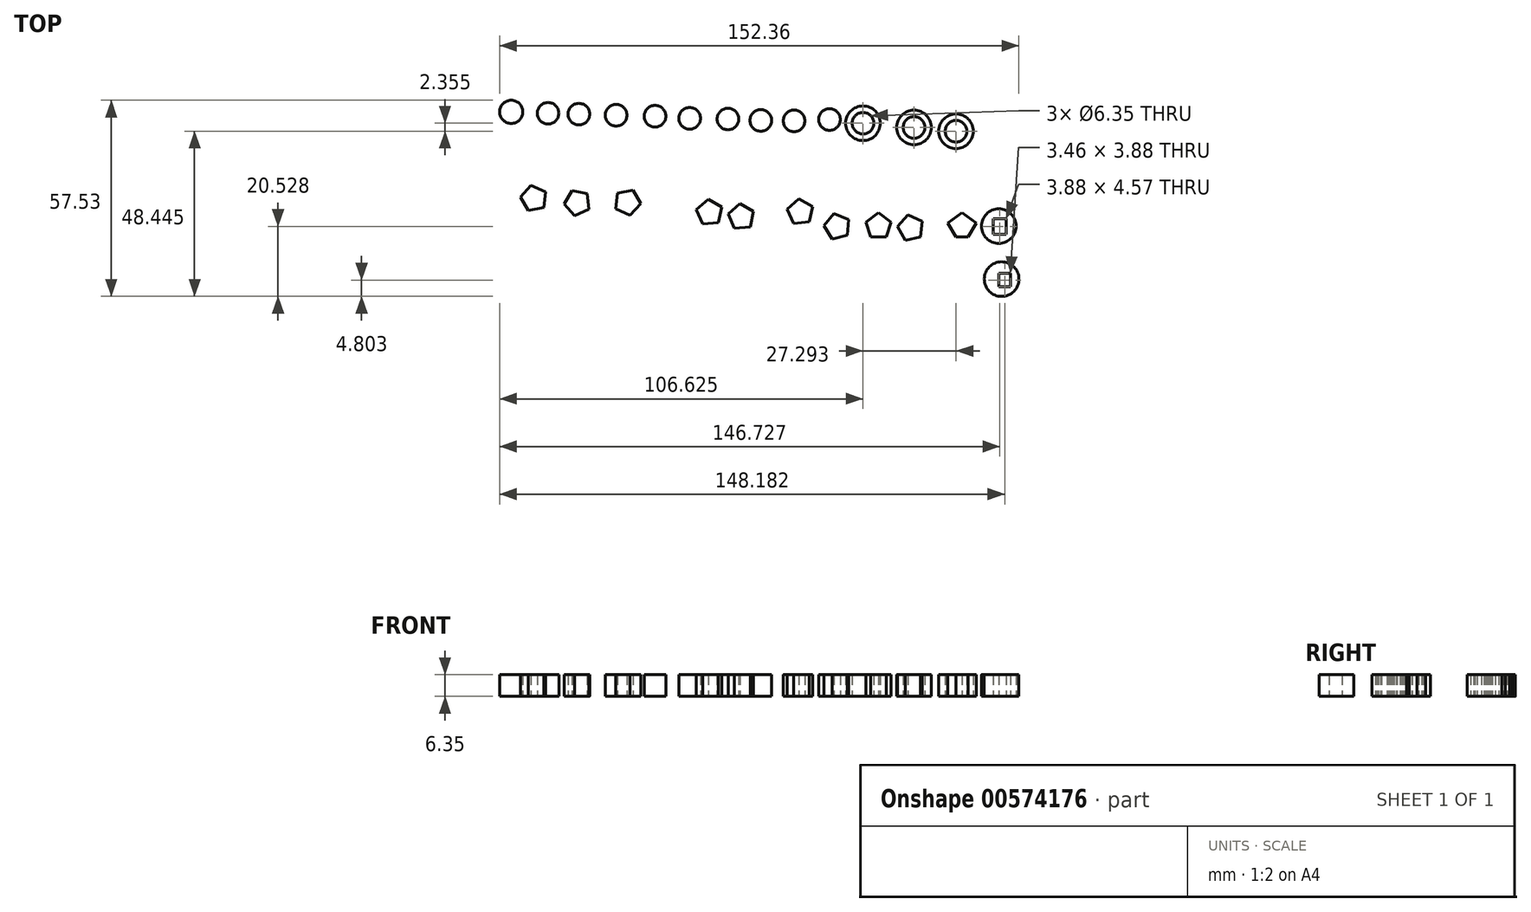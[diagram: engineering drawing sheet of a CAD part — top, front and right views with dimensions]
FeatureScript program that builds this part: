
annotation { "Feature Type Name" : "Feature", "Feature Type Description" : "" }
export const myFeature = defineFeature(function(context is Context, id is Id, definition is map)
    precondition{}
    {
        {
            var Q0;
            Q0=qCreatedBy(makeId("Top.planeOp"),FACE);
            var sketch = newSketch(context, id + "F0", { "sketchPlane" : qUnion([Q0])});
            skCircle(sketch, "E0", {"center": v(-53.37, 48.39) * mm, "radius": 3.18 * mm});
            skCircle(sketch, "E1", {"center": v(-42.44, 48.08) * mm, "radius": 3.18 * mm});
            skCircle(sketch, "E2", {"center": v(-31.04, 47.77) * mm, "radius": 3.18 * mm});
            skCircle(sketch, "E3", {"center": v(-20.87, 47.15) * mm, "radius": 3.18 * mm});
            skCircle(sketch, "E4", {"center": v(-62.41, 48.63) * mm, "radius": 3.18 * mm});
            skCircle(sketch, "E5", {"center": v(-9.63, 46.97) * mm, "radius": 3.18 * mm});
            skCircle(sketch, "E6", {"center": v(0, 46.55) * mm, "radius": 3.18 * mm});
            skCircle(sketch, "E7", {"center": v(9.77, 46.41) * mm, "radius": 3.18 * mm});
            skCircle(sketch, "E8", {"center": v(20.16, 46.83) * mm, "radius": 3.18 * mm});
            skCircle(sketch, "E9", {"center": v(30, 45.72) * mm, "radius": 5.08 * mm});
            skCircle(sketch, "E10", {"center": v(30, 45.72) * mm, "radius": 3.18 * mm});
            skCircle(sketch, "E11", {"center": v(44.96, 44.47) * mm, "radius": 3.18 * mm});
            skCircle(sketch, "E12", {"center": v(44.96, 44.47) * mm, "radius": 5.08 * mm});
            skCircle(sketch, "E13", {"center": v(57.29, 43.36) * mm, "radius": 3.18 * mm});
            skCircle(sketch, "E14", {"center": v(57.29, 43.36) * mm, "radius": 5.08 * mm});
            skCircle(sketch, "E15.cCircle", {"center": v(-66.58, 23.66) * mm, "radius": 3.18 * mm, "construction": true});
            skLineSegment(sketch, "E15.0", {"start": v(-63.66, 21.03) * mm, "end": v(-68.18, 20.07) * mm});
            skLineSegment(sketch, "E15.1", {"start": v(-68.18, 20.07) * mm, "end": v(-70.48, 24.07) * mm});
            skLineSegment(sketch, "E15.2", {"start": v(-70.48, 24.07) * mm, "end": v(-67.4, 27.5) * mm});
            skLineSegment(sketch, "E15.3", {"start": v(-67.4, 27.5) * mm, "end": v(-63.18, 25.62) * mm});
            skLineSegment(sketch, "E15.4", {"start": v(-63.18, 25.62) * mm, "end": v(-63.66, 21.03) * mm});
            skPoint(sketch, "E15.0.midPoint", {"position": v(-65.92, 20.55) * mm});
            skCircle(sketch, "E16", {"center": v(-73.22, 49.05) * mm, "radius": 3.4 * mm});
            skCircle(sketch, "E17.cCircle", {"center": v(-53.82, 22.42) * mm, "radius": 3.18 * mm, "construction": true});
            skLineSegment(sketch, "E17.0", {"start": v(-50.44, 20.43) * mm, "end": v(-54.67, 18.59) * mm});
            skLineSegment(sketch, "E17.1", {"start": v(-54.67, 18.59) * mm, "end": v(-57.73, 22.03) * mm});
            skLineSegment(sketch, "E17.2", {"start": v(-57.73, 22.03) * mm, "end": v(-55.4, 26.01) * mm});
            skLineSegment(sketch, "E17.3", {"start": v(-55.4, 26.01) * mm, "end": v(-50.9, 25.03) * mm});
            skLineSegment(sketch, "E17.4", {"start": v(-50.9, 25.03) * mm, "end": v(-50.44, 20.43) * mm});
            skPoint(sketch, "E17.0.midPoint", {"position": v(-52.55, 19.5) * mm});
            skCircle(sketch, "E18.cCircle", {"center": v(-39.14, 22.58) * mm, "radius": 3.17 * mm, "construction": true});
            skLineSegment(sketch, "E18.0", {"start": v(-38.38, 18.73) * mm, "end": v(-42.57, 20.67) * mm});
            skLineSegment(sketch, "E18.1", {"start": v(-42.57, 20.67) * mm, "end": v(-42.02, 25.25) * mm});
            skLineSegment(sketch, "E18.2", {"start": v(-42.02, 25.25) * mm, "end": v(-37.49, 26.14) * mm});
            skLineSegment(sketch, "E18.3", {"start": v(-37.49, 26.14) * mm, "end": v(-35.24, 22.11) * mm});
            skLineSegment(sketch, "E18.4", {"start": v(-35.24, 22.11) * mm, "end": v(-38.38, 18.73) * mm});
            skPoint(sketch, "E18.0.midPoint", {"position": v(-40.47, 19.7) * mm});
            skCircle(sketch, "E19.cCircle", {"center": v(-15.05, 19.5) * mm, "radius": 3.18 * mm, "construction": true});
            skLineSegment(sketch, "E19.0", {"start": v(-12.44, 16.58) * mm, "end": v(-17.03, 16.12) * mm});
            skLineSegment(sketch, "E19.1", {"start": v(-17.03, 16.12) * mm, "end": v(-18.88, 20.35) * mm});
            skLineSegment(sketch, "E19.2", {"start": v(-18.88, 20.35) * mm, "end": v(-15.43, 23.42) * mm});
            skLineSegment(sketch, "E19.3", {"start": v(-15.43, 23.42) * mm, "end": v(-11.45, 21.08) * mm});
            skLineSegment(sketch, "E19.4", {"start": v(-11.45, 21.08) * mm, "end": v(-12.44, 16.58) * mm});
            skPoint(sketch, "E19.0.midPoint", {"position": v(-14.73, 16.35) * mm});
            skCircle(sketch, "E20.cCircle", {"center": v(-5.72, 18.24) * mm, "radius": 3.18 * mm, "construction": true});
            skPoint(sketch, "E20.cCircle.centerSnap0", {"position": v(-17.95, 18.24) * mm});
            skLineSegment(sketch, "E20.0", {"start": v(-3.1, 15.3) * mm, "end": v(-7.7, 14.85) * mm});
            skLineSegment(sketch, "E20.1", {"start": v(-7.7, 14.85) * mm, "end": v(-9.55, 19.08) * mm});
            skLineSegment(sketch, "E20.2", {"start": v(-9.55, 19.08) * mm, "end": v(-6.1, 22.14) * mm});
            skLineSegment(sketch, "E20.3", {"start": v(-6.1, 22.14) * mm, "end": v(-2.12, 19.81) * mm});
            skLineSegment(sketch, "E20.4", {"start": v(-2.12, 19.81) * mm, "end": v(-3.1, 15.3) * mm});
            skPoint(sketch, "E20.0.midPoint", {"position": v(-5.4, 15.08) * mm});
            skCircle(sketch, "E21.cCircle", {"center": v(34.54, 15.5) * mm, "radius": 3.17 * mm, "construction": true});
            skLineSegment(sketch, "E21.0", {"start": v(36.84, 12.33) * mm, "end": v(32.23, 12.33) * mm});
            skLineSegment(sketch, "E21.1", {"start": v(32.23, 12.33) * mm, "end": v(30.8, 16.72) * mm});
            skLineSegment(sketch, "E21.2", {"start": v(30.8, 16.72) * mm, "end": v(34.54, 19.43) * mm});
            skLineSegment(sketch, "E21.3", {"start": v(34.54, 19.43) * mm, "end": v(38.27, 16.72) * mm});
            skLineSegment(sketch, "E21.4", {"start": v(38.27, 16.72) * mm, "end": v(36.84, 12.33) * mm});
            skPoint(sketch, "E21.0.midPoint", {"position": v(34.54, 12.33) * mm});
            skCircle(sketch, "E22.cCircle", {"center": v(43.96, 14.98) * mm, "radius": 3.18 * mm, "construction": true});
            skLineSegment(sketch, "E22.0", {"start": v(46.86, 12.33) * mm, "end": v(42.35, 11.4) * mm});
            skLineSegment(sketch, "E22.1", {"start": v(42.35, 11.4) * mm, "end": v(40.06, 15.4) * mm});
            skLineSegment(sketch, "E22.2", {"start": v(40.06, 15.4) * mm, "end": v(43.17, 18.82) * mm});
            skLineSegment(sketch, "E22.3", {"start": v(43.17, 18.82) * mm, "end": v(47.37, 16.92) * mm});
            skLineSegment(sketch, "E22.4", {"start": v(47.37, 16.92) * mm, "end": v(46.86, 12.33) * mm});
            skPoint(sketch, "E22.0.midPoint", {"position": v(44.93, 12.33) * mm});
            skCircle(sketch, "E23.cCircle", {"center": v(11.59, 19.7) * mm, "radius": 3.18 * mm, "construction": true});
            skLineSegment(sketch, "E23.0", {"start": v(14.2, 16.77) * mm, "end": v(9.6, 16.32) * mm});
            skLineSegment(sketch, "E23.1", {"start": v(9.6, 16.32) * mm, "end": v(7.76, 20.54) * mm});
            skLineSegment(sketch, "E23.2", {"start": v(7.76, 20.54) * mm, "end": v(11.2, 23.6) * mm});
            skLineSegment(sketch, "E23.3", {"start": v(11.2, 23.6) * mm, "end": v(15.19, 21.28) * mm});
            skLineSegment(sketch, "E23.4", {"start": v(15.19, 21.28) * mm, "end": v(14.2, 16.77) * mm});
            skPoint(sketch, "E23.0.midPoint", {"position": v(11.9, 16.54) * mm});
            skCircle(sketch, "E24.cCircle", {"center": v(22.4, 15.4) * mm, "radius": 3.18 * mm, "construction": true});
            skLineSegment(sketch, "E24.0", {"start": v(25.41, 12.9) * mm, "end": v(20.94, 11.76) * mm});
            skLineSegment(sketch, "E24.1", {"start": v(20.94, 11.76) * mm, "end": v(18.48, 15.67) * mm});
            skLineSegment(sketch, "E24.2", {"start": v(18.48, 15.67) * mm, "end": v(21.43, 19.21) * mm});
            skLineSegment(sketch, "E24.3", {"start": v(21.43, 19.21) * mm, "end": v(25.71, 17.5) * mm});
            skLineSegment(sketch, "E24.4", {"start": v(25.71, 17.5) * mm, "end": v(25.41, 12.9) * mm});
            skPoint(sketch, "E24.0.midPoint", {"position": v(23.18, 12.33) * mm});
            skCircle(sketch, "E25.cCircle", {"center": v(59.05, 15.5) * mm, "radius": 3.18 * mm, "construction": true});
            skLineSegment(sketch, "E25.0", {"start": v(60.86, 12.33) * mm, "end": v(57.24, 12.33) * mm});
            skLineSegment(sketch, "E25.1", {"start": v(57.24, 12.33) * mm, "end": v(54.84, 16.37) * mm});
            skLineSegment(sketch, "E25.2", {"start": v(54.84, 16.37) * mm, "end": v(59.05, 19.43) * mm});
            skLineSegment(sketch, "E25.3", {"start": v(59.05, 19.43) * mm, "end": v(63.26, 16.37) * mm});
            skLineSegment(sketch, "E25.4", {"start": v(63.26, 16.37) * mm, "end": v(60.86, 12.33) * mm});
            skPoint(sketch, "E25.0.midPoint", {"position": v(59.05, 12.33) * mm});
            skCircle(sketch, "E26", {"center": v(69.82, 15.52) * mm, "radius": 5.08 * mm});
            skCircle(sketch, "E27", {"center": v(70.65, 0) * mm, "radius": 5.08 * mm});
            skLineSegment(sketch, "E28.bottom", {"start": v(68.16, 17.73) * mm, "end": v(72.04, 17.73) * mm});
            skLineSegment(sketch, "E28.top", {"start": v(68.16, 13.16) * mm, "end": v(72.04, 13.16) * mm});
            skLineSegment(sketch, "E28.left", {"start": v(68.16, 17.73) * mm, "end": v(68.16, 13.16) * mm});
            skLineSegment(sketch, "E28.right", {"start": v(72.04, 17.73) * mm, "end": v(72.04, 13.16) * mm});
            skLineSegment(sketch, "E29.bottom", {"start": v(69.82, 1.66) * mm, "end": v(73.28, 1.66) * mm});
            skLineSegment(sketch, "E29.top", {"start": v(69.82, -2.22) * mm, "end": v(73.28, -2.22) * mm});
            skLineSegment(sketch, "E29.left", {"start": v(69.82, 1.66) * mm, "end": v(69.82, -2.22) * mm});
            skLineSegment(sketch, "E29.right", {"start": v(73.28, 1.66) * mm, "end": v(73.28, -2.22) * mm});
            skSolve(sketch);
        }
        {
            var Q0;
            Q0 = qSketchRegion(id + "F0", true);
            extrude(context, id + "F1", {"entities" : qUnion([Q0]), "depth" : 6.35 * mm, "offsetDistance" : 25.4 * mm});
        }
    });
